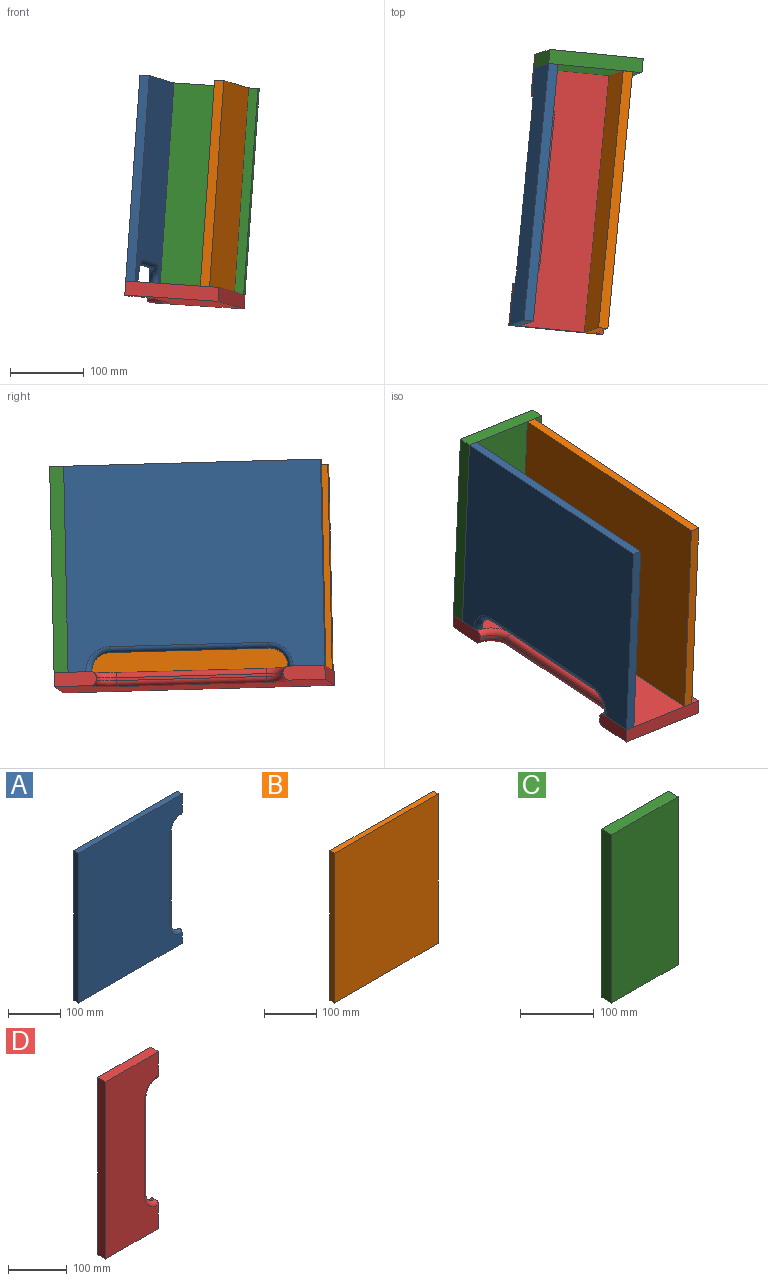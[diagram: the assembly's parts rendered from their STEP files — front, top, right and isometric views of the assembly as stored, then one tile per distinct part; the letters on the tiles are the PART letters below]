
ASSEMBLY  parts=4 mates=3
PART A: 13 faces, bbox 279.4x12.7x349.3 mm
  f0: plane 31.64x12.7mm, normal (1,0,0), area 378.4mm2, adj f4,f5,f6,f7,f8
  f1: plane 50.69x12.7mm, normal (1,0,0), area 620.3mm2, adj f2,f5,f6,f11,f12
  f2: plane 279.4x12.7mm, normal (0,0,1), area 3548.4mm2, adj f1,f3,f5,f6
  f3: plane 349.25x12.7mm, normal (-1,0,0), area 4435.5mm2, adj f2,f4,f5,f6
  f4: plane 279.4x12.7mm, normal (0,0,-1), area 3548.4mm2, adj f0,f3,f5,f6
  f5: plane 349.25x279.4mm, normal (0,-1,0), area 88738.8mm2, adj f0,f1,f2,f3,f4,f7,f9,f11
  f6: plane 349.25x279.4mm, normal (0,1,0), area 88738.8mm2, adj f0,f1,f2,f3,f4,f8,f10,f12
  f7: torus R=33.02mm, axis (0,-1,0), area 478.6mm2, adj f0,f5,f8,f9
  f8: torus R=33.02mm, axis (0,-1,0), area 478.6mm2, adj f0,f6,f7,f10
  f9: cylinder r=7.62mm len=215.9mm, axis (0,0,-1), area 2308.7mm2, adj f5,f7,f10,f11
  f10: cylinder r=7.62mm len=215.9mm, axis (0,0,1), area 2308.7mm2, adj f6,f8,f9,f12
  f11: torus R=33.02mm, axis (0,-1,0), area 478.6mm2, adj f1,f5,f9,f12
  f12: torus R=33.02mm, axis (0,-1,0), area 478.6mm2, adj f1,f6,f10,f11
PART B: 6 faces, bbox 279.4x12.7x349.3 mm
  f0: plane 349.25x12.7mm, normal (-1,0,0), area 4435.5mm2, adj f1,f3,f4,f5
  f1: plane 279.4x12.7mm, normal (0,0,-1), area 3548.4mm2, adj f0,f2,f4,f5
  f2: plane 349.25x12.7mm, normal (1,0,0), area 4435.5mm2, adj f1,f3,f4,f5
  f3: plane 279.4x12.7mm, normal (0,0,1), area 3548.4mm2, adj f0,f2,f4,f5
  f4: plane 349.25x279.4mm, normal (0,-1,0), area 97580.4mm2, adj f0,f1,f2,f3
  f5: plane 349.25x279.4mm, normal (0,1,0), area 97580.4mm2, adj f0,f1,f2,f3
PART C: 6 faces, bbox 127x19.1x279.4 mm
  f0: plane 279.4x19.05mm, normal (-1,0,0), area 5322.6mm2, adj f1,f3,f4,f5
  f1: plane 127x19.05mm, normal (0,0,-1), area 2419.3mm2, adj f0,f2,f4,f5
  f2: plane 279.4x19.05mm, normal (1,0,0), area 5322.6mm2, adj f1,f3,f4,f5
  f3: plane 127x19.05mm, normal (0,0,1), area 2419.3mm2, adj f0,f2,f4,f5
  f4: plane 279.4x127mm, normal (0,-1,0), area 35483.8mm2, adj f0,f1,f2,f3
  f5: plane 279.4x127mm, normal (0,1,0), area 35483.8mm2, adj f0,f1,f2,f3
PART D: 16 faces, bbox 127x19.1x368.3 mm
  f0: plane 57.15x19.05mm, normal (1,0,0), area 1063.8mm2, adj f1,f7,f8,f9,f10,f13
  f1: cylinder r=25.4mm len=25.4mm, axis (0,1,0), area 152mm2, adj f0,f2,f10,f13
  f2: plane 203.2x3.81mm, normal (1,0,0), area 774.2mm2, adj f1,f3,f11,f14
  f3: cylinder r=25.4mm len=25.4mm, axis (0,1,0), area 152mm2, adj f2,f4,f12,f15
  f4: plane 57.15x19.05mm, normal (1,0,0), area 1063.8mm2, adj f3,f5,f8,f9,f12,f15
  f5: plane 127x19.05mm, normal (0,0,1), area 2419.3mm2, adj f4,f6,f8,f9
  f6: plane 368.3x19.05mm, normal (-1,0,0), area 7016.1mm2, adj f5,f7,f8,f9
  f7: plane 127x19.05mm, normal (0,0,-1), area 2419.3mm2, adj f0,f6,f8,f9
  f8: plane 368.3x127mm, normal (0,-1,0), area 38351.8mm2, adj f0,f4,f5,f6,f7,f13,f14,f15
  f9: plane 368.3x127mm, normal (0,1,0), area 38351.8mm2, adj f0,f4,f5,f6,f7,f10,f11,f12
  f10: torus R=33.02mm, axis (0,-1,0), area 529.6mm2, adj f0,f1,f9,f11
  f11: cylinder r=7.62mm len=203.2mm, axis (0,0,1), area 2432.2mm2, adj f2,f9,f10,f12
  f12: torus R=33.02mm, axis (0,-1,0), area 529.6mm2, adj f3,f4,f9,f11
  f13: torus R=33.02mm, axis (0,-1,0), area 529.6mm2, adj f0,f1,f8,f14
  f14: cylinder r=7.62mm len=203.2mm, axis (0,0,-1), area 2432.2mm2, adj f2,f8,f13,f15
  f15: torus R=33.02mm, axis (0,-1,0), area 529.6mm2, adj f3,f4,f8,f14
PLACE A rot(axis=(0.56,0.55,-0.62),124.7deg) t=(5.28,74.65,-190.97)mm
PLACE B rot(axis=(-0.54,0.63,0.56),120deg) t=(89.5,23.9,-195.7)mm
PLACE C rot(axis=(-0.2,0.56,-0.8),6.9deg) t=(96.46,238.38,-222.2)mm
PLACE D rot(axis=(0.06,0.71,0.7),178.8deg) t=(25.27,-55.1,-310.06)mm
MATE fastened B.f2 <-> D.f9  axis (-0.07,-0.02,-1) through (79.11,-132.62,-312.12)mm
MATE fastened D.f9 <-> A.f1  axis (0.07,0.02,1) through (-34.39,-121.47,-304.51)mm
MATE fastened D.f9 <-> C.f1  axis (0.07,0.02,1) through (0.92,244.99,-314.8)mm
